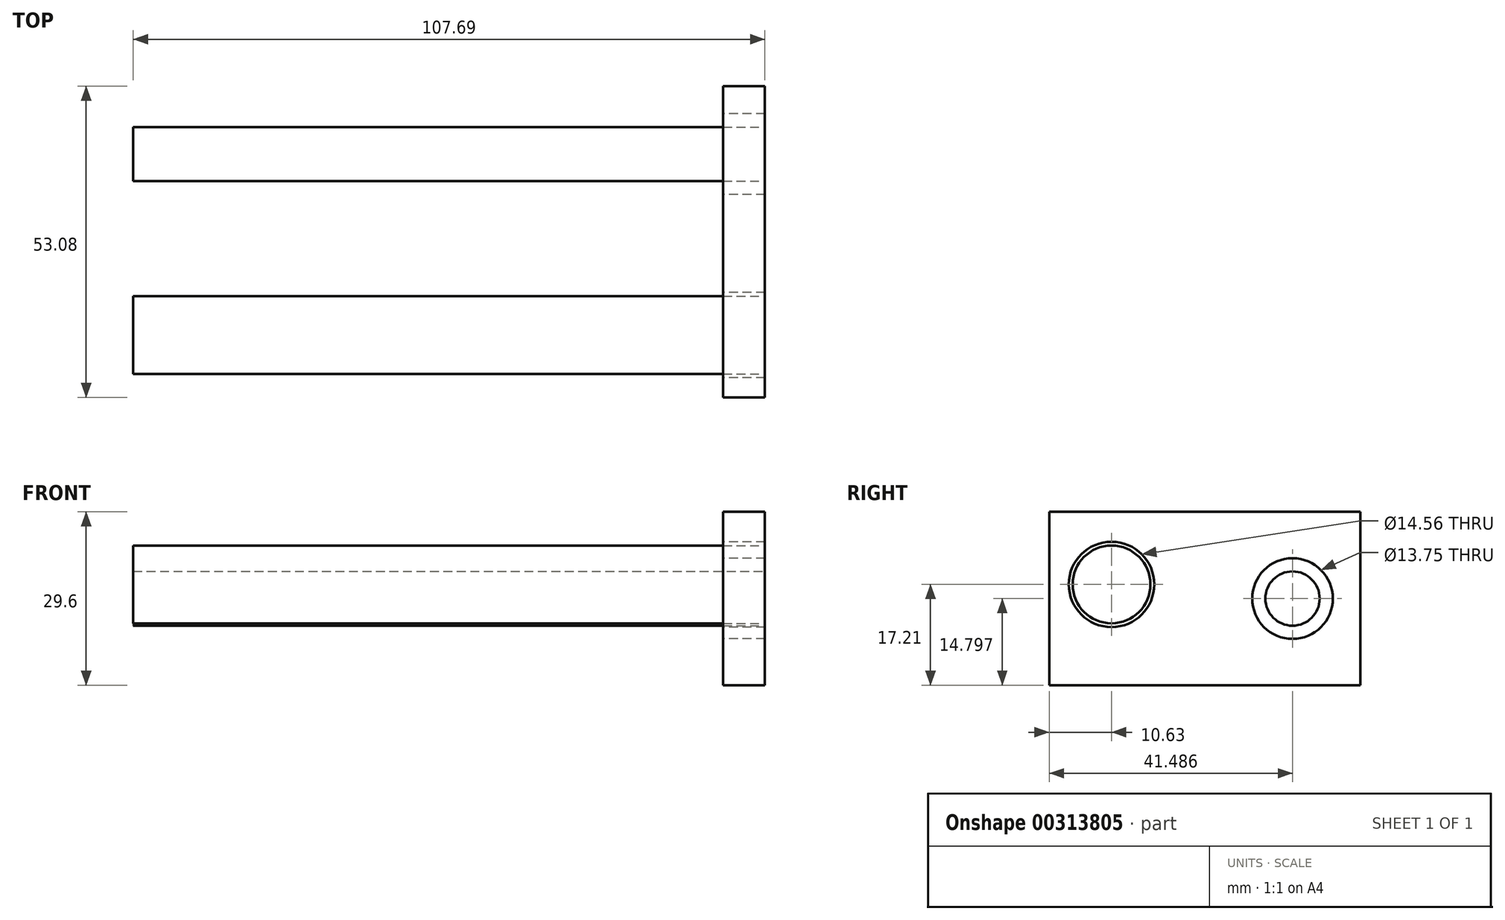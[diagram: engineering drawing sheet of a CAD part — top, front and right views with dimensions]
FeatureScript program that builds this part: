
annotation { "Feature Type Name" : "Feature", "Feature Type Description" : "" }
export const myFeature = defineFeature(function(context is Context, id is Id, definition is map)
    precondition{}
    {
        {
            var Q0;
            Q0=qCreatedBy(makeId("Right.planeOp"),FACE);
            var sketch = newSketch(context, id + "F0", { "sketchPlane" : qUnion([Q0])});
            skLineSegment(sketch, "E0.bottom", {"start": v(-108.28, 55.67) * mm, "end": v(-55.2, 55.67) * mm});
            skLineSegment(sketch, "E0.top", {"start": v(-108.28, 26.07) * mm, "end": v(-55.2, 26.07) * mm});
            skLineSegment(sketch, "E0.left", {"start": v(-108.28, 55.67) * mm, "end": v(-108.28, 26.07) * mm});
            skLineSegment(sketch, "E0.right", {"start": v(-55.2, 55.67) * mm, "end": v(-55.2, 26.07) * mm});
            skCircle(sketch, "E1", {"center": v(-97.65, 43.28) * mm, "radius": 7.28 * mm});
            skCircle(sketch, "E2", {"center": v(-66.8, 40.87) * mm, "radius": 6.87 * mm});
            skPoint(sketch, "E2.centerSnap0", {"position": v(-55.2, 40.87) * mm});
            skSolve(sketch);
        }
        {
            var Q0;
            Q0 = qSketchRegion(id + "F0", true);
            extrude(context, id + "F1", {"entities" : qUnion([Q0]), "depth" : 7.11 * mm});
        }
        {
            var Q0;
            Q0=makeQuery(id+"F1.opExtrude","CAP_FACE",FACE,{"disambiguationData":[OSD([sQuery(id+"F0.wireOp",EDGE,"E0.bottom"),sQuery(id+"F0.wireOp",EDGE,"E0.top"),sQuery(id+"F0.wireOp",EDGE,"E0.left"),sQuery(id+"F0.wireOp",EDGE,"E0.right"),sQuery(id+"F0.wireOp",EDGE,"E1"),sQuery(id+"F0.wireOp",EDGE,"E2")])],"isStart":false});
            var sketch = newSketch(context, id + "F2", { "sketchPlane" : qUnion([Q0])});
            skCircle(sketch, "E3", {"center": v(-66.8, 40.87) * mm, "radius": 4.63 * mm});
            skCircle(sketch, "E4", {"center": v(-97.65, 43.28) * mm, "radius": 6.63 * mm});
            skSolve(sketch);
        }
        {
            var Q0;
            Q0=makeQuery(id+"F2.imprint","IMPRINT",FACE,{"disambiguationData":[TD([[makeQuery(id+"F2.imprint","IMPRINT",EDGE,{"derivedFrom":sQuery(id+"F2.wireOp",EDGE,"E4")}),1.0]])]});
            var Q1;
            Q1=makeQuery(id+"F2.imprint","IMPRINT",FACE,{"disambiguationData":[TD([[makeQuery(id+"F2.imprint","IMPRINT",EDGE,{"derivedFrom":sQuery(id+"F2.wireOp",EDGE,"E3")}),1.0]])]});
            extrude(context, id + "F3", {"entities" : qUnion([Q0, Q1]), "oppositeDirection" : true, "depth" : 107.7 * mm});
        }
    });
